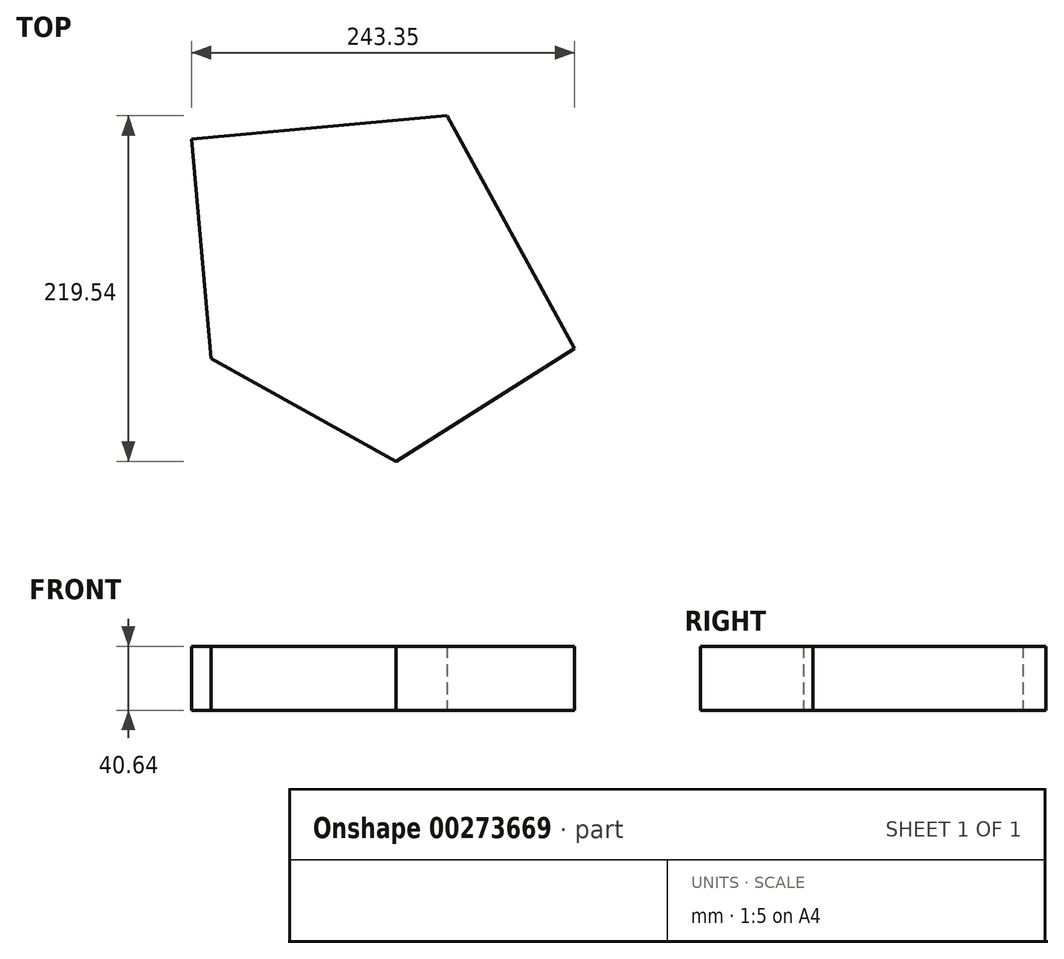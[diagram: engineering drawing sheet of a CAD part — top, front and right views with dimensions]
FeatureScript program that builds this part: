
annotation { "Feature Type Name" : "Feature", "Feature Type Description" : "" }
export const myFeature = defineFeature(function(context is Context, id is Id, definition is map)
    precondition{}
    {
        {
            var Q0;
            Q0=qCreatedBy(makeId("Top.planeOp"),FACE);
            var sketch = newSketch(context, id + "F0", { "sketchPlane" : qUnion([Q0])});
            skLineSegment(sketch, "E0", {"start": v(0, -71.49) * mm, "end": v(113.35, 0) * mm});
            skLineSegment(sketch, "E1", {"start": v(113.35, 0) * mm, "end": v(32.51, 148.05) * mm});
            skLineSegment(sketch, "E2", {"start": v(32.51, 148.05) * mm, "end": v(-130, 133.26) * mm});
            skLineSegment(sketch, "E3", {"start": v(-130, 133.26) * mm, "end": v(-117.32, -6.1) * mm});
            skLineSegment(sketch, "E4", {"start": v(-117.32, -6.1) * mm, "end": v(0, -71.49) * mm});
            skSolve(sketch);
        }
        {
            var Q0;
            Q0=makeQuery(id+"F0.imprint","IMPRINT",FACE,{"disambiguationData":[TD([[makeQuery(id+"F0.imprint","IMPRINT",EDGE,{"derivedFrom":sQuery(id+"F0.wireOp",EDGE,"E0")}),1.0]])]});
            extrude(context, id + "F1", {"entities" : qUnion([Q0]), "depth" : 40.64 * mm});
        }
    });
